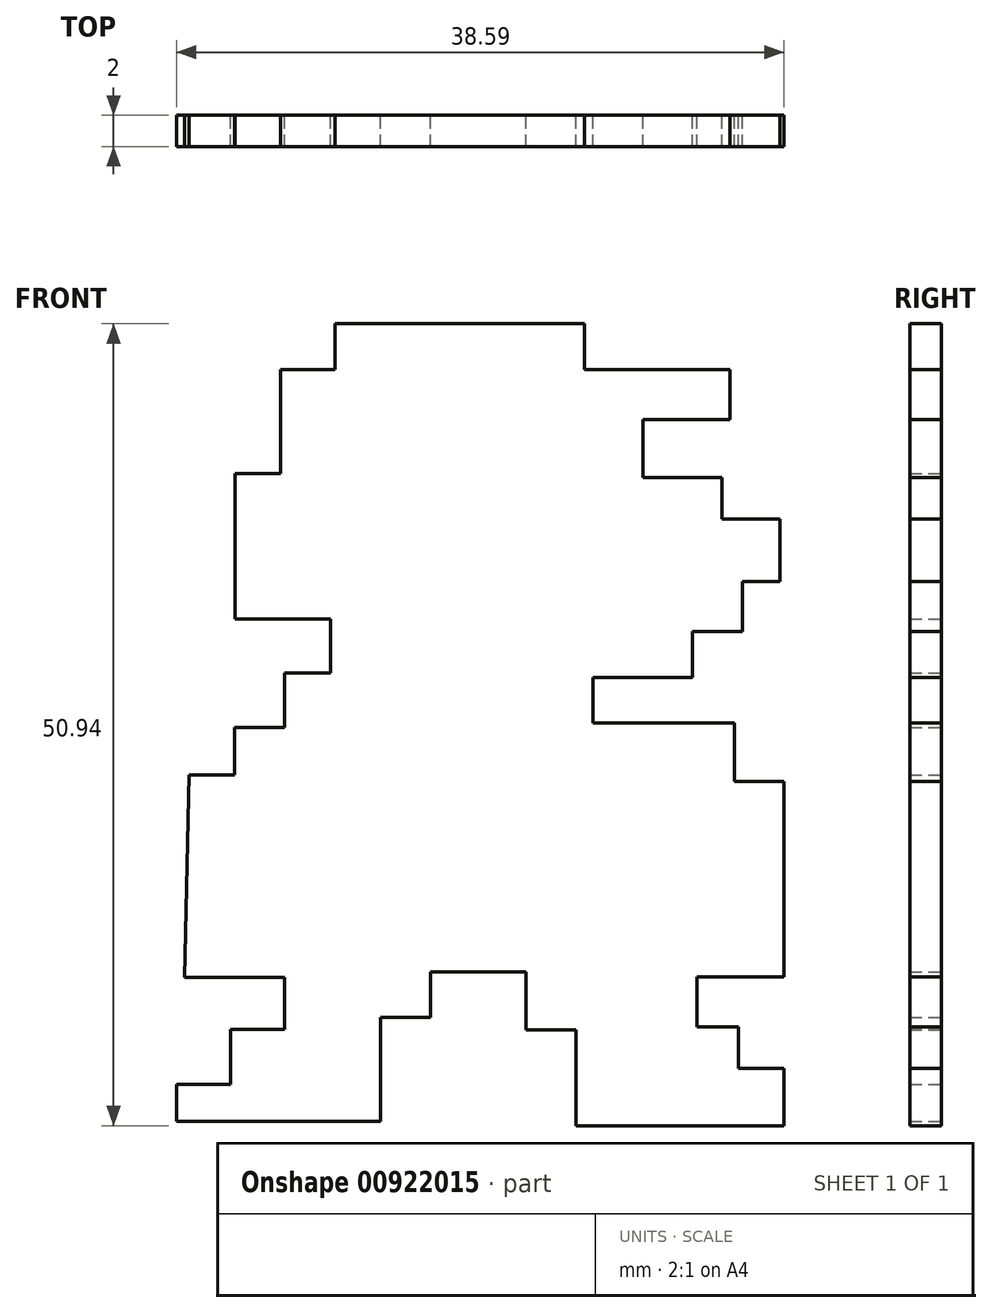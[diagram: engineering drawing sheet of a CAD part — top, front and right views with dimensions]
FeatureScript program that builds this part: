
annotation { "Feature Type Name" : "Feature", "Feature Type Description" : "" }
export const myFeature = defineFeature(function(context is Context, id is Id, definition is map)
    precondition{}
    {
        {
            var Q0;
            Q0=qCreatedBy(makeId("Front.planeOp"),FACE);
            var sketch = newSketch(context, id + "F0", { "sketchPlane" : qUnion([Q0])});
            skLineSegment(sketch, "E0", {"start": v(-33.39, 54.16) * mm, "end": v(-33.39, 57.07) * mm});
            skLineSegment(sketch, "E1", {"start": v(-33.39, 57.07) * mm, "end": v(-17.55, 57.07) * mm});
            skLineSegment(sketch, "E2", {"start": v(-17.55, 57.07) * mm, "end": v(-17.55, 54.16) * mm});
            skLineSegment(sketch, "E3", {"start": v(-17.55, 54.16) * mm, "end": v(-8.3, 54.16) * mm});
            skLineSegment(sketch, "E4", {"start": v(-8.3, 54.16) * mm, "end": v(-8.3, 51) * mm});
            skLineSegment(sketch, "E5", {"start": v(-36.84, 51) * mm, "end": v(-36.84, 54.16) * mm});
            skLineSegment(sketch, "E6", {"start": v(-36.84, 54.16) * mm, "end": v(-33.39, 54.16) * mm});
            skLineSegment(sketch, "E7", {"start": v(-13.85, 51) * mm, "end": v(-13.85, 47.3) * mm});
            skLineSegment(sketch, "E8", {"start": v(-13.85, 47.3) * mm, "end": v(-8.83, 47.3) * mm});
            skLineSegment(sketch, "E9", {"start": v(-8.83, 47.3) * mm, "end": v(-8.83, 44.65) * mm});
            skLineSegment(sketch, "E10", {"start": v(-8.83, 44.65) * mm, "end": v(-5.13, 44.65) * mm});
            skLineSegment(sketch, "E11", {"start": v(-5.13, 44.65) * mm, "end": v(-5.13, 40.69) * mm});
            skLineSegment(sketch, "E12", {"start": v(-5.13, 40.69) * mm, "end": v(-7.51, 40.69) * mm});
            skLineSegment(sketch, "E13", {"start": v(-7.51, 40.69) * mm, "end": v(-7.51, 37.52) * mm});
            skLineSegment(sketch, "E14", {"start": v(-7.51, 37.52) * mm, "end": v(-10.68, 37.52) * mm});
            skLineSegment(sketch, "E15", {"start": v(-10.68, 37.52) * mm, "end": v(-10.68, 34.6) * mm});
            skLineSegment(sketch, "E16", {"start": v(-10.68, 34.6) * mm, "end": v(-17.02, 34.6) * mm});
            skLineSegment(sketch, "E17", {"start": v(-17.02, 34.6) * mm, "end": v(-17.02, 31.7) * mm});
            skLineSegment(sketch, "E18", {"start": v(-17.02, 31.7) * mm, "end": v(-8.04, 31.7) * mm});
            skLineSegment(sketch, "E19", {"start": v(-8.04, 31.7) * mm, "end": v(-8.04, 28) * mm});
            skLineSegment(sketch, "E20", {"start": v(-8.04, 28) * mm, "end": v(-4.87, 28) * mm});
            skLineSegment(sketch, "E21", {"start": v(-4.87, 28) * mm, "end": v(-4.87, 15.58) * mm});
            skLineSegment(sketch, "E22", {"start": v(-4.87, 15.58) * mm, "end": v(-10.42, 15.58) * mm});
            skLineSegment(sketch, "E23", {"start": v(-10.42, 15.58) * mm, "end": v(-10.42, 12.41) * mm});
            skLineSegment(sketch, "E24", {"start": v(-10.42, 12.41) * mm, "end": v(-7.77, 12.41) * mm});
            skLineSegment(sketch, "E25", {"start": v(-7.77, 12.41) * mm, "end": v(-7.77, 9.77) * mm});
            skLineSegment(sketch, "E26", {"start": v(-7.77, 9.77) * mm, "end": v(-4.88, 9.77) * mm});
            skLineSegment(sketch, "E27", {"start": v(-4.88, 9.77) * mm, "end": v(-4.88, 6.13) * mm});
            skLineSegment(sketch, "E28", {"start": v(-4.88, 6.13) * mm, "end": v(-18.1, 6.13) * mm});
            skLineSegment(sketch, "E29", {"start": v(-18.1, 12.2) * mm, "end": v(-18.1, 6.13) * mm});
            skLineSegment(sketch, "E30", {"start": v(-21.26, 12.2) * mm, "end": v(-18.1, 12.2) * mm});
            skLineSegment(sketch, "E31", {"start": v(-21.26, 15.9) * mm, "end": v(-21.26, 12.2) * mm});
            skLineSegment(sketch, "E32", {"start": v(-21.26, 15.9) * mm, "end": v(-27.34, 15.9) * mm});
            skLineSegment(sketch, "E33", {"start": v(-27.34, 15.9) * mm, "end": v(-27.34, 13) * mm});
            skLineSegment(sketch, "E34", {"start": v(-27.34, 13) * mm, "end": v(-30.51, 13) * mm});
            skLineSegment(sketch, "E35", {"start": v(-30.51, 13) * mm, "end": v(-30.51, 6.39) * mm});
            skLineSegment(sketch, "E36", {"start": v(-30.51, 6.39) * mm, "end": v(-43.46, 6.39) * mm});
            skLineSegment(sketch, "E37", {"start": v(-43.46, 6.39) * mm, "end": v(-43.46, 8.77) * mm});
            skLineSegment(sketch, "E38", {"start": v(-40.03, 8.77) * mm, "end": v(-43.46, 8.77) * mm});
            skLineSegment(sketch, "E39", {"start": v(-40.03, 12.24) * mm, "end": v(-40.03, 8.77) * mm});
            skLineSegment(sketch, "E40", {"start": v(-40.03, 12.24) * mm, "end": v(-36.6, 12.24) * mm});
            skLineSegment(sketch, "E41", {"start": v(-36.6, 12.24) * mm, "end": v(-36.6, 15.56) * mm});
            skLineSegment(sketch, "E42", {"start": v(-42.94, 15.56) * mm, "end": v(-36.6, 15.56) * mm});
            skLineSegment(sketch, "E43", {"start": v(-42.68, 28.4) * mm, "end": v(-42.94, 15.56) * mm});
            skLineSegment(sketch, "E44", {"start": v(-39.77, 28.4) * mm, "end": v(-42.68, 28.4) * mm});
            skPoint(sketch, "E44.startSnap0", {"position": v(-39.77, 15.56) * mm});
            skLineSegment(sketch, "E45", {"start": v(-39.77, 31.42) * mm, "end": v(-39.77, 28.4) * mm});
            skLineSegment(sketch, "E46", {"start": v(-36.6, 31.42) * mm, "end": v(-39.77, 31.42) * mm});
            skLineSegment(sketch, "E47", {"start": v(-36.6, 34.87) * mm, "end": v(-36.6, 31.42) * mm});
            skLineSegment(sketch, "E48", {"start": v(-33.67, 34.87) * mm, "end": v(-36.6, 34.87) * mm});
            skLineSegment(sketch, "E49", {"start": v(-33.67, 38.3) * mm, "end": v(-33.67, 34.87) * mm});
            skLineSegment(sketch, "E50", {"start": v(-39.75, 38.3) * mm, "end": v(-33.67, 38.3) * mm});
            skLineSegment(sketch, "E51", {"start": v(-39.75, 47.55) * mm, "end": v(-39.75, 38.3) * mm});
            skLineSegment(sketch, "E52", {"start": v(-36.84, 47.55) * mm, "end": v(-39.75, 47.55) * mm});
            skLineSegment(sketch, "E53", {"start": v(-36.84, 51) * mm, "end": v(-36.84, 47.55) * mm});
            skLineSegment(sketch, "E54", {"start": v(-27.34, 15.9) * mm, "end": v(-21.26, 15.9) * mm});
            skLineSegment(sketch, "E55", {"start": v(-17.55, 54.16) * mm, "end": v(-17.55, 57.07) * mm});
            skLineSegment(sketch, "E56", {"start": v(-13.85, 51) * mm, "end": v(-8.3, 51) * mm});
            skSolve(sketch);
        }
        {
            var Q0;
            Q0 = qSketchRegion(id + "F0", true);
            extrude(context, id + "F1", {"entities" : qUnion([Q0]), "depth" : 2 * mm, "offsetDistance" : 25 * mm});
        }
    });
